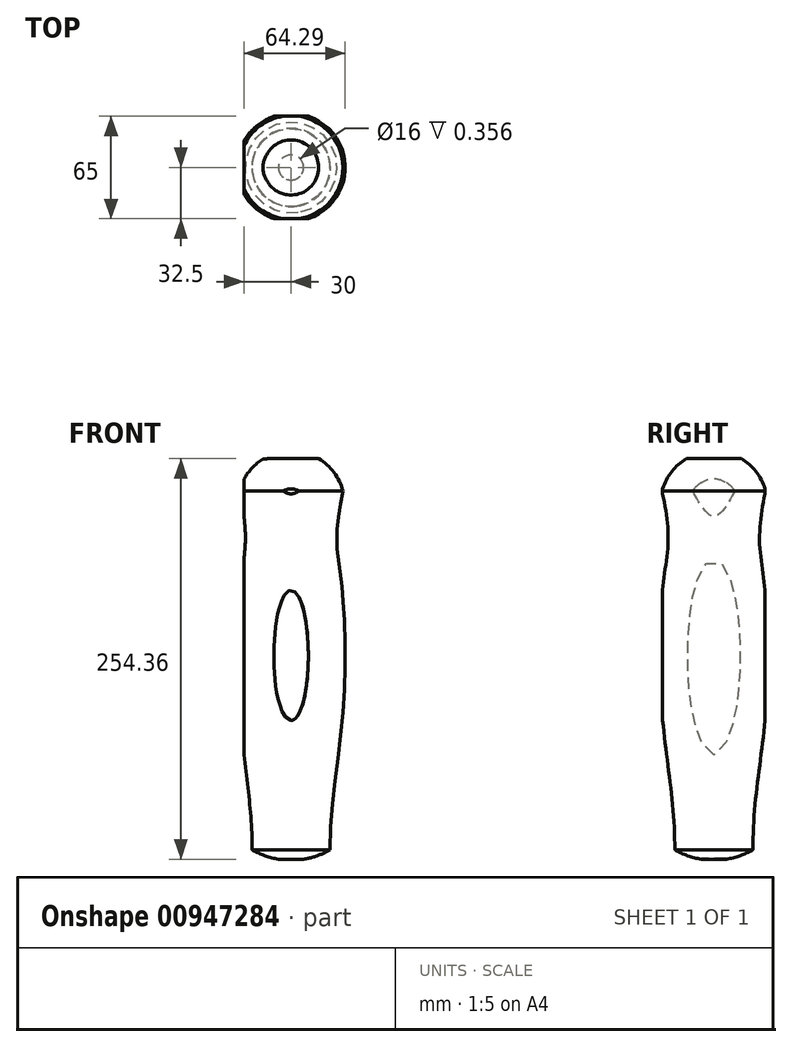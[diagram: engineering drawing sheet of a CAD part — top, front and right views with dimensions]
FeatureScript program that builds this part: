
annotation { "Feature Type Name" : "Feature", "Feature Type Description" : "" }
export const myFeature = defineFeature(function(context is Context, id is Id, definition is map)
    precondition{}
    {
        {
            var Q0;
            Q0=qCreatedBy(makeId("Top.planeOp"),FACE);
            var sketch = newSketch(context, id + "F0", { "sketchPlane" : qUnion([Q0])});
            skLineSegment(sketch, "E0.bottom", {"start": v(-20, 32.5) * mm, "end": v(25, 32.5) * mm});
            skLineSegment(sketch, "E0.top", {"start": v(-20, -32.5) * mm, "end": v(25, -32.5) * mm});
            skLineSegment(sketch, "E0.left", {"start": v(-30, 22.5) * mm, "end": v(-30, -22.5) * mm});
            skLineSegment(sketch, "E0.right", {"start": v(35, 22.5) * mm, "end": v(35, -22.5) * mm});
            skPoint(sketch, "E1.visualSharp", {"position": v(-30, 32.5) * mm});
            skArc(sketch, "E1.filletArc", {"start": v(-20, 32.5) * mm, "mid": v(-27.07, 29.57) * mm, "end": v(-30, 22.5) * mm});
            skPoint(sketch, "E2.visualSharp", {"position": v(35, 32.5) * mm});
            skArc(sketch, "E2.filletArc", {"start": v(35, 22.5) * mm, "mid": v(32.07, 29.57) * mm, "end": v(25, 32.5) * mm});
            skPoint(sketch, "E3.visualSharp", {"position": v(35, -32.5) * mm});
            skArc(sketch, "E3.filletArc", {"start": v(25, -32.5) * mm, "mid": v(32.07, -29.57) * mm, "end": v(35, -22.5) * mm});
            skPoint(sketch, "E4.visualSharp", {"position": v(-30, -32.5) * mm});
            skArc(sketch, "E4.filletArc", {"start": v(-30, -22.5) * mm, "mid": v(-27.07, -29.57) * mm, "end": v(-20, -32.5) * mm});
            skSolve(sketch);
        }
        {
            var Q0;
            Q0 = qSketchRegion(id + "F0", true);
            extrude(context, id + "F1", {"entities" : qUnion([Q0]), "depth" : 255 * mm, "offsetDistance" : 25 * mm});
        }
        {
            var Q0;
            Q0=makeQuery(id+"F1.opExtrude","CAP_EDGE",EDGE,{"disambiguationData":[OSD([sQuery(id+"F0.wireOp",EDGE,"E0.left")])],"isStart":true});
            fillet(context, id + "F2", {"entities" : qUnion([Q0]), "tangentPropagation" : true, "radius" : 15 * mm, "defaultsChanged" : true, "vertexSettings" : [], "allowEdgeOverflow" : false});
        }
        {
            var Q0;
            Q0=makeQuery(id+"F1.opExtrude","CAP_EDGE",EDGE,{"disambiguationData":[OSD([sQuery(id+"F0.wireOp",EDGE,"E0.left")])],"isStart":false});
            fillet(context, id + "F3", {"entities" : qUnion([Q0]), "tangentPropagation" : true, "radius" : 15 * mm, "defaultsChanged" : true, "vertexSettings" : [], "allowEdgeOverflow" : false});
        }
        {
            var Q0;
            Q0=qCreatedBy(makeId("Right.planeOp"),FACE);
            var sketch = newSketch(context, id + "F4", { "sketchPlane" : qUnion([Q0])});
            skLineSegment(sketch, "E5", {"start": v(0, 0) * mm, "end": v(0, 288.74) * mm, "construction": true});
            skFitSpline(sketch, "E6", {"points": [v(-25, 0) * mm, v(-32.89, 93.25) * mm, v(-32, 176.38) * mm, v(-29, 205) * mm, v(-33.73, 237.96) * mm, v(-60.78, 269.53) * mm], "startDerivative": vector(15.23, 365.15) * mm, "endDerivative": vector(-352.95, 212.12) * mm});
            skLineSegment(sketch, "E7", {"start": v(-39.93, 257) * mm, "end": v(-81.63, 257) * mm});
            skLineSegment(sketch, "E8", {"start": v(-81.63, 257) * mm, "end": v(-81.63, 0) * mm});
            skLineSegment(sketch, "E9", {"start": v(-81.63, 0) * mm, "end": v(-25, 0) * mm});
            skPoint(sketch, "E10", {"position": v(-60.78, 257) * mm});
            skSolve(sketch);
        }
        {
            var Q0;
            Q0 = qSketchRegion(id + "F4", true);
            var Q1;
            Q1=sQuery(id+"F4.wireOp",EDGE,"E5");
            revolve(context, id + "F5", {"operationType" : NewBodyOperationType.REMOVE, "surfaceOperationType" : NewSurfaceOperationType.NEW, "entities" : qUnion([Q0]), "axis" : qUnion([Q1]), "revolveType" : RevolveType.FULL, "oppositeDirection" : true});
        }
        {
            var Q0;
            Q0=makeQuery(id+"F1.opExtrude","CAP_FACE",FACE,{"disambiguationData":[OSD([sQuery(id+"F0.wireOp",EDGE,"E0.bottom"),sQuery(id+"F0.wireOp",EDGE,"E0.top"),sQuery(id+"F0.wireOp",EDGE,"E0.left"),sQuery(id+"F0.wireOp",EDGE,"E0.right"),sQuery(id+"F0.wireOp",EDGE,"E1.filletArc"),sQuery(id+"F0.wireOp",EDGE,"E2.filletArc"),sQuery(id+"F0.wireOp",EDGE,"E3.filletArc"),sQuery(id+"F0.wireOp",EDGE,"E4.filletArc")])],"isStart":true});
            var sketch = newSketch(context, id + "F6", { "sketchPlane" : qUnion([Q0])});
            skCircle(sketch, "E11", {"center": v(0, 0) * mm, "radius": 8 * mm});
            skSolve(sketch);
        }
        {
            var Q0;
            Q0 = qSketchRegion(id + "F6", true);
            extrude(context, id + "F7", {"entities" : qUnion([Q0]), "operationType" : NewBodyOperationType.REMOVE, "oppositeDirection" : true, "depth" : 1 * mm, "offsetDistance" : 25 * mm});
        }
        {
            var Q0;
            Q0=qCreatedBy(makeId("Right.planeOp"),FACE);
            var sketch = newSketch(context, id + "F8", { "sketchPlane" : qUnion([Q0])});
            skArc(sketch, "E12", {"start": v(0, 259.85) * mm, "mid": v(-24.04, 249.89) * mm, "end": v(-34, 225.85) * mm});
            skLineSegment(sketch, "E13", {"start": v(-34, 225.85) * mm, "end": v(-96, 225.85) * mm});
            skLineSegment(sketch, "E14", {"start": v(-96, 291.85) * mm, "end": v(0, 291.85) * mm});
            skLineSegment(sketch, "E15", {"start": v(0, 291.85) * mm, "end": v(0, 259.85) * mm});
            skLineSegment(sketch, "E16", {"start": v(-96, 291.85) * mm, "end": v(-96, 225.85) * mm});
            skLineSegment(sketch, "E17", {"start": v(0, 241.3) * mm, "end": v(0, 200.98) * mm, "construction": true});
            skSolve(sketch);
        }
        {
            var Q0;
            Q0=makeQuery(id+"F8.imprint","IMPRINT",FACE,{"disambiguationData":[TD([[makeQuery(id+"F8.imprint","IMPRINT",EDGE,{"derivedFrom":sQuery(id+"F8.wireOp",EDGE,"E12")}),-1.0]])]});
            var Q1;
            Q1=sQuery(id+"F8.wireOp",EDGE,"E14");
            var Q2;
            Q2=sQuery(id+"F8.wireOp",EDGE,"E17");
            revolve(context, id + "F9", {"operationType" : NewBodyOperationType.REMOVE, "surfaceOperationType" : NewSurfaceOperationType.NEW, "entities" : qUnion([Q0]), "surfaceEntities" : qUnion([Q1]), "axis" : qUnion([Q2]), "revolveType" : RevolveType.FULL, "oppositeDirection" : true});
        }
        {
            var Q0;
            Q0=qCreatedBy(makeId("Right.planeOp"),FACE);
            var sketch = newSketch(context, id + "F10", { "sketchPlane" : qUnion([Q0])});
            skArc(sketch, "E18", {"start": v(-50, 50) * mm, "mid": v(-35.36, 14.64) * mm, "end": v(0, 0) * mm});
            skLineSegment(sketch, "E19", {"start": v(-50, 50) * mm, "end": v(-50, -21.79) * mm});
            skLineSegment(sketch, "E20", {"start": v(0, -21.79) * mm, "end": v(-50, -21.79) * mm});
            skLineSegment(sketch, "E21", {"start": v(0, 0) * mm, "end": v(0, -21.79) * mm});
            skPoint(sketch, "E22.start.orphan", {"position": v(50, 50) * mm});
            skSolve(sketch);
        }
        {
            var Q0;
            Q0=qCreatedBy(makeId("Right.planeOp"),FACE);
            var sketch = newSketch(context, id + "F11", { "sketchPlane" : qUnion([Q0])});
            skLineSegment(sketch, "E23", {"start": v(0, 0) * mm, "end": v(0, 69.18) * mm, "construction": true});
            skSolve(sketch);
        }
        {
            var Q0;
            Q0 = qSketchRegion(id + "F10", true);
            var Q1;
            Q1=sQuery(id+"F11.wireOp",EDGE,"E23");
            revolve(context, id + "F12", {"operationType" : NewBodyOperationType.REMOVE, "surfaceOperationType" : NewSurfaceOperationType.NEW, "entities" : qUnion([Q0]), "axis" : qUnion([Q1]), "revolveType" : RevolveType.FULL, "oppositeDirection" : true});
        }
    });
